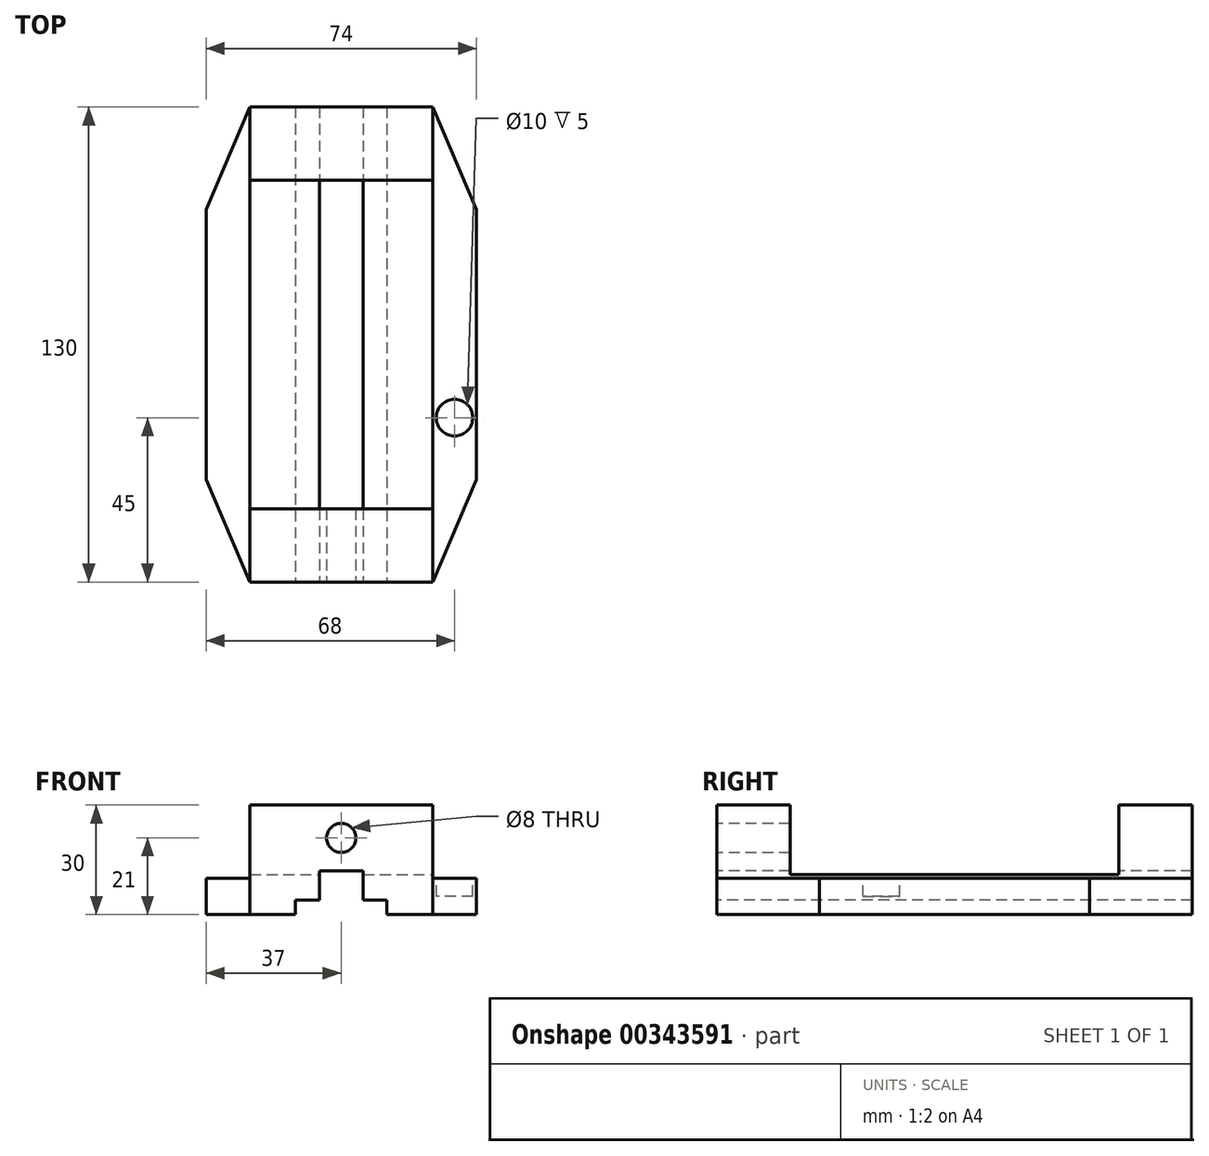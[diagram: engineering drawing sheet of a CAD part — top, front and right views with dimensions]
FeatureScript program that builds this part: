
annotation { "Feature Type Name" : "Feature", "Feature Type Description" : "" }
export const myFeature = defineFeature(function(context is Context, id is Id, definition is map)
    precondition{}
    {
        {
            var Q0;
            Q0=qCreatedBy(makeId("Top.planeOp"),FACE);
            var sketch = newSketch(context, id + "F0", { "sketchPlane" : qUnion([Q0])});
            skLineSegment(sketch, "E0.bottom", {"start": v(25, 65) * mm, "end": v(-25, 65) * mm});
            skLineSegment(sketch, "E0.top", {"start": v(25, -65) * mm, "end": v(-25, -65) * mm});
            skLineSegment(sketch, "E0.left", {"start": v(37, 37) * mm, "end": v(37, -37) * mm});
            skLineSegment(sketch, "E0.right", {"start": v(-37, 37) * mm, "end": v(-37, -37) * mm});
            skPoint(sketch, "E0.middle", {"position": v(0, 0) * mm});
            skLineSegment(sketch, "E1", {"start": v(37, -37) * mm, "end": v(25, -65) * mm});
            skLineSegment(sketch, "E2", {"start": v(0, 0) * mm, "end": v(0, -42.44) * mm, "construction": true});
            skLineSegment(sketch, "E3.MirrorCS", {"start": v(-37, -37) * mm, "end": v(-25, -65) * mm});
            skPoint(sketch, "E4.orphan", {"position": v(-37, -65) * mm});
            skPoint(sketch, "E5.orphan", {"position": v(37, -65) * mm});
            skLineSegment(sketch, "E6", {"start": v(0, 0) * mm, "end": v(24.98, 0) * mm, "construction": true});
            skLineSegment(sketch, "E7.MirrorCS", {"start": v(-37, 37) * mm, "end": v(-25, 65) * mm});
            skLineSegment(sketch, "E8.MirrorCS", {"start": v(37, 37) * mm, "end": v(25, 65) * mm});
            skPoint(sketch, "E9.orphan", {"position": v(-37, 65) * mm});
            skPoint(sketch, "E10.orphan", {"position": v(37, 65) * mm});
            skSolve(sketch);
        }
        {
            var Q0;
            Q0 = qSketchRegion(id + "F0", true);
            extrude(context, id + "F1", {"entities" : qUnion([Q0]), "depth" : 30 * mm});
        }
        {
            var Q0;
            Q0=makeQuery(id+"F1.opExtrude","CAP_FACE",FACE,{"disambiguationData":[OSD([sQuery(id+"F0.wireOp",EDGE,"E0.bottom"),sQuery(id+"F0.wireOp",EDGE,"E0.top"),sQuery(id+"F0.wireOp",EDGE,"E0.left"),sQuery(id+"F0.wireOp",EDGE,"E0.right"),sQuery(id+"F0.wireOp",EDGE,"E1"),sQuery(id+"F0.wireOp",EDGE,"E3.MirrorCS"),sQuery(id+"F0.wireOp",EDGE,"E7.MirrorCS"),sQuery(id+"F0.wireOp",EDGE,"E8.MirrorCS")])],"isStart":false});
            var sketch = newSketch(context, id + "F2", { "sketchPlane" : qUnion([Q0])});
            skLineSegment(sketch, "E11.bottom", {"start": v(25, -65) * mm, "end": v(37, -65) * mm});
            skLineSegment(sketch, "E11.top", {"start": v(25, 65) * mm, "end": v(37, 65) * mm});
            skLineSegment(sketch, "E11.left", {"start": v(25, -65) * mm, "end": v(25, 65) * mm});
            skLineSegment(sketch, "E11.right", {"start": v(37, -65) * mm, "end": v(37, 65) * mm});
            skLineSegment(sketch, "E12", {"start": v(0, 0) * mm, "end": v(0, -38.77) * mm, "construction": true});
            skLineSegment(sketch, "E13.MirrorCS", {"start": v(-25, 65) * mm, "end": v(-37, 65) * mm});
            skLineSegment(sketch, "E14.MirrorCS", {"start": v(-25, -65) * mm, "end": v(-25, 65) * mm});
            skLineSegment(sketch, "E15.MirrorCS", {"start": v(-37, -65) * mm, "end": v(-37, 65) * mm});
            skLineSegment(sketch, "E16.MirrorCS", {"start": v(-25, -65) * mm, "end": v(-37, -65) * mm});
            skSolve(sketch);
        }
        {
            var Q0;
            Q0 = qSketchRegion(id + "F2", true);
            extrude(context, id + "F3", {"entities" : qUnion([Q0]), "operationType" : NewBodyOperationType.REMOVE, "oppositeDirection" : true, "depth" : 20 * mm});
        }
        {
            var Q0;
            Q0=makeQuery(id+"F1.opExtrude","CAP_FACE",FACE,{"disambiguationData":[OSD([sQuery(id+"F0.wireOp",EDGE,"E0.bottom"),sQuery(id+"F0.wireOp",EDGE,"E0.top"),sQuery(id+"F0.wireOp",EDGE,"E0.left"),sQuery(id+"F0.wireOp",EDGE,"E0.right"),sQuery(id+"F0.wireOp",EDGE,"E1"),sQuery(id+"F0.wireOp",EDGE,"E3.MirrorCS"),sQuery(id+"F0.wireOp",EDGE,"E7.MirrorCS"),sQuery(id+"F0.wireOp",EDGE,"E8.MirrorCS")])],"isStart":false});
            var sketch = newSketch(context, id + "F4", { "sketchPlane" : qUnion([Q0])});
            skLineSegment(sketch, "E17.bottom", {"start": v(-25, 45) * mm, "end": v(25, 45) * mm});
            skLineSegment(sketch, "E17.top", {"start": v(-25, -45) * mm, "end": v(25, -45) * mm});
            skLineSegment(sketch, "E17.left", {"start": v(-25, 45) * mm, "end": v(-25, -45) * mm});
            skLineSegment(sketch, "E17.right", {"start": v(25, 45) * mm, "end": v(25, -45) * mm});
            skSolve(sketch);
        }
        {
            var Q0;
            Q0 = qSketchRegion(id + "F4", true);
            extrude(context, id + "F5", {"entities" : qUnion([Q0]), "operationType" : NewBodyOperationType.REMOVE, "oppositeDirection" : true, "depth" : 19 * mm});
        }
        {
            var Q0;
            Q0=makeQuery(id+"F1.opExtrude","SWEPT_FACE",FACE,{"disambiguationData":[OSD([sQuery(id+"F0.wireOp",EDGE,"E0.top")])]});
            var sketch = newSketch(context, id + "F6", { "sketchPlane" : qUnion([Q0])});
            skLineSegment(sketch, "E18.bottom", {"start": v(-12.5, 0) * mm, "end": v(12.5, 0) * mm});
            skLineSegment(sketch, "E18.top", {"start": v(-12.5, 4) * mm, "end": v(-6, 4) * mm});
            skLineSegment(sketch, "E18.left", {"start": v(-12.5, 0) * mm, "end": v(-12.5, 4) * mm});
            skLineSegment(sketch, "E18.right", {"start": v(12.5, 0) * mm, "end": v(12.5, 4) * mm});
            skLineSegment(sketch, "E19", {"start": v(-6, 4) * mm, "end": v(-6, 12) * mm});
            skLineSegment(sketch, "E20", {"start": v(-6, 12) * mm, "end": v(6, 12) * mm});
            skLineSegment(sketch, "E21", {"start": v(6, 12) * mm, "end": v(6, 4) * mm});
            skLineSegment(sketch, "E22.trimOffspring", {"start": v(6, 4) * mm, "end": v(12.5, 4) * mm});
            skSolve(sketch);
        }
        {
            var Q0;
            Q0=makeQuery(id+"F6.imprint","IMPRINT",FACE,{"disambiguationData":[TD([[makeQuery(id+"F6.imprint","IMPRINT",EDGE,{"derivedFrom":sQuery(id+"F6.wireOp",EDGE,"E18.bottom")}),-1.0]])]});
            extrude(context, id + "F7", {"entities" : qUnion([Q0]), "operationType" : NewBodyOperationType.REMOVE, "endBound" : BoundingType.THROUGH_ALL, "oppositeDirection" : true, "depth" : 25 * mm});
        }
        {
            var Q0;
            Q0=makeQuery(id+"F1.opExtrude","SWEPT_FACE",FACE,{"disambiguationData":[OSD([sQuery(id+"F0.wireOp",EDGE,"E0.top")])]});
            var sketch = newSketch(context, id + "F8", { "sketchPlane" : qUnion([Q0])});
            skCircle(sketch, "E23", {"center": v(0, 21) * mm, "radius": 4 * mm});
            skSolve(sketch);
        }
        {
            var Q0;
            Q0 = qSketchRegion(id + "F8", true);
            extrude(context, id + "F9", {"entities" : qUnion([Q0]), "operationType" : NewBodyOperationType.REMOVE, "endBound" : BoundingType.UP_TO_NEXT, "oppositeDirection" : true, "depth" : 25 * mm});
        }
        {
            var Q0;
            Q0=makeQuery(id+"F3.boolean.opBoolean","COPY",FACE,{"derivedFrom":makeQuery(id+"F3.opExtrude","CAP_FACE",FACE,{"disambiguationData":[OSD([sQuery(id+"F2.wireOp",EDGE,"E11.bottom"),sQuery(id+"F2.wireOp",EDGE,"E11.top"),sQuery(id+"F2.wireOp",EDGE,"E11.left"),sQuery(id+"F2.wireOp",EDGE,"E11.right")])],"isStart":false})});
            var sketch = newSketch(context, id + "F10", { "sketchPlane" : qUnion([Q0])});
            skCircle(sketch, "E24", {"center": v(31, -20) * mm, "radius": 5 * mm});
            skSolve(sketch);
        }
        {
            var Q0;
            Q0 = qSketchRegion(id + "F10", true);
            extrude(context, id + "F11", {"entities" : qUnion([Q0]), "operationType" : NewBodyOperationType.REMOVE, "oppositeDirection" : true, "depth" : 5 * mm});
        }
    });
